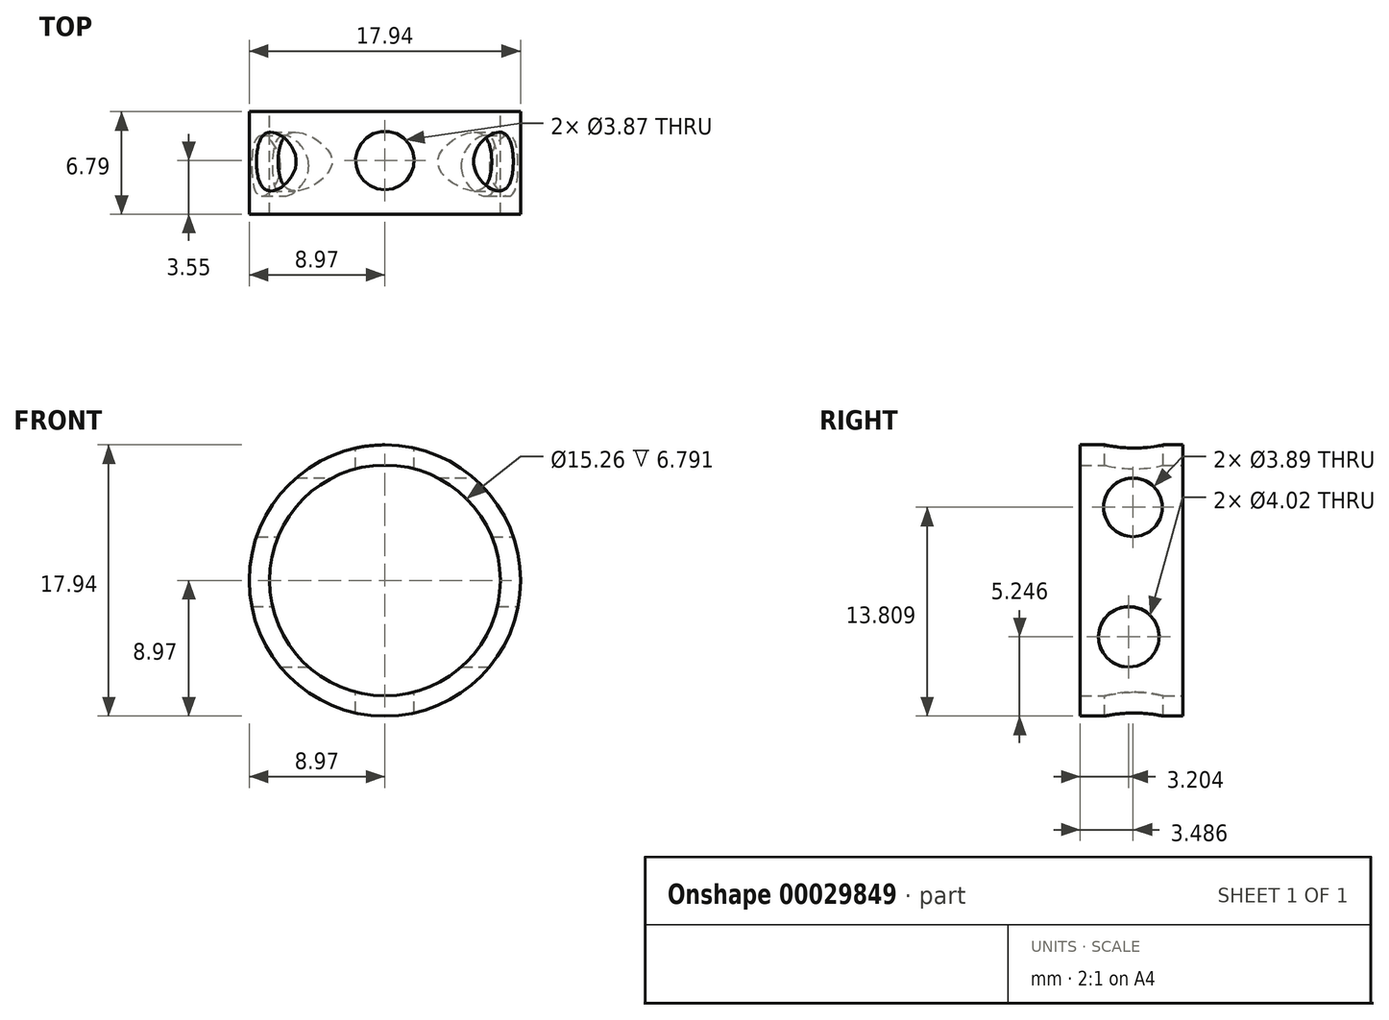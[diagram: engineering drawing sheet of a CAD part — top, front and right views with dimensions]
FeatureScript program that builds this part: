
annotation { "Feature Type Name" : "Feature", "Feature Type Description" : "" }
export const myFeature = defineFeature(function(context is Context, id is Id, definition is map)
    precondition{}
    {
        {
            var Q0;
            Q0=qCreatedBy(makeId("Front.planeOp"),FACE);
            var sketch = newSketch(context, id + "F0", { "sketchPlane" : qUnion([Q0])});
            skCircle(sketch, "E0", {"center": v(0, 0) * mm, "radius": 7.63 * mm});
            skCircle(sketch, "E1", {"center": v(0, 0) * mm, "radius": 8.97 * mm});
            skSolve(sketch);
        }
        {
            var Q0;
            Q0=makeQuery(id+"F0.imprint","IMPRINT",FACE,{"disambiguationData":[TD([[makeQuery(id+"F0.imprint","IMPRINT",EDGE,{"derivedFrom":sQuery(id+"F0.wireOp",EDGE,"E0")}),-1.0]])]});
            extrude(context, id + "F1", {"entities" : qUnion([Q0]), "depth" : 6.8 * mm});
        }
        {
            var Q0;
            Q0=qCreatedBy(makeId("Top.planeOp"),FACE);
            var sketch = newSketch(context, id + "F2", { "sketchPlane" : qUnion([Q0])});
            skCircle(sketch, "E2", {"center": v(0, -3.24) * mm, "radius": 1.94 * mm});
            skSolve(sketch);
        }
        {
            var Q0;
            Q0=makeQuery(id+"F2.imprint","IMPRINT",FACE,{"disambiguationData":[TD([[makeQuery(id+"F2.imprint","IMPRINT",EDGE,{"derivedFrom":sQuery(id+"F2.wireOp",EDGE,"E2")}),1.0]])]});
            extrude(context, id + "F3", {"entities" : qUnion([Q0]), "operationType" : NewBodyOperationType.REMOVE, "endBound" : BoundingType.SYMMETRIC, "oppositeDirection" : true, "depth" : 28.2 * mm});
        }
        {
            var Q0;
            Q0=qCreatedBy(makeId("Right.planeOp"),FACE);
            var sketch = newSketch(context, id + "F4", { "sketchPlane" : qUnion([Q0])});
            skCircle(sketch, "E3", {"center": v(-3.3, 4.84) * mm, "radius": 1.95 * mm});
            skSolve(sketch);
        }
        {
            var Q0;
            Q0 = qSketchRegion(id + "F4", true);
            extrude(context, id + "F5", {"entities" : qUnion([Q0]), "operationType" : NewBodyOperationType.REMOVE, "endBound" : BoundingType.SYMMETRIC, "oppositeDirection" : true, "depth" : 25 * mm});
        }
        {
            var Q0;
            Q0=qCreatedBy(makeId("Right.planeOp"),FACE);
            var sketch = newSketch(context, id + "F6", { "sketchPlane" : qUnion([Q0])});
            skCircle(sketch, "E4", {"center": v(-3.59, -3.72) * mm, "radius": 2 * mm});
            skSolve(sketch);
        }
        {
            var Q0;
            Q0 = qSketchRegion(id + "F6", true);
            extrude(context, id + "F7", {"entities" : qUnion([Q0]), "operationType" : NewBodyOperationType.REMOVE, "endBound" : BoundingType.SYMMETRIC, "oppositeDirection" : true, "depth" : 25 * mm});
        }
    });
